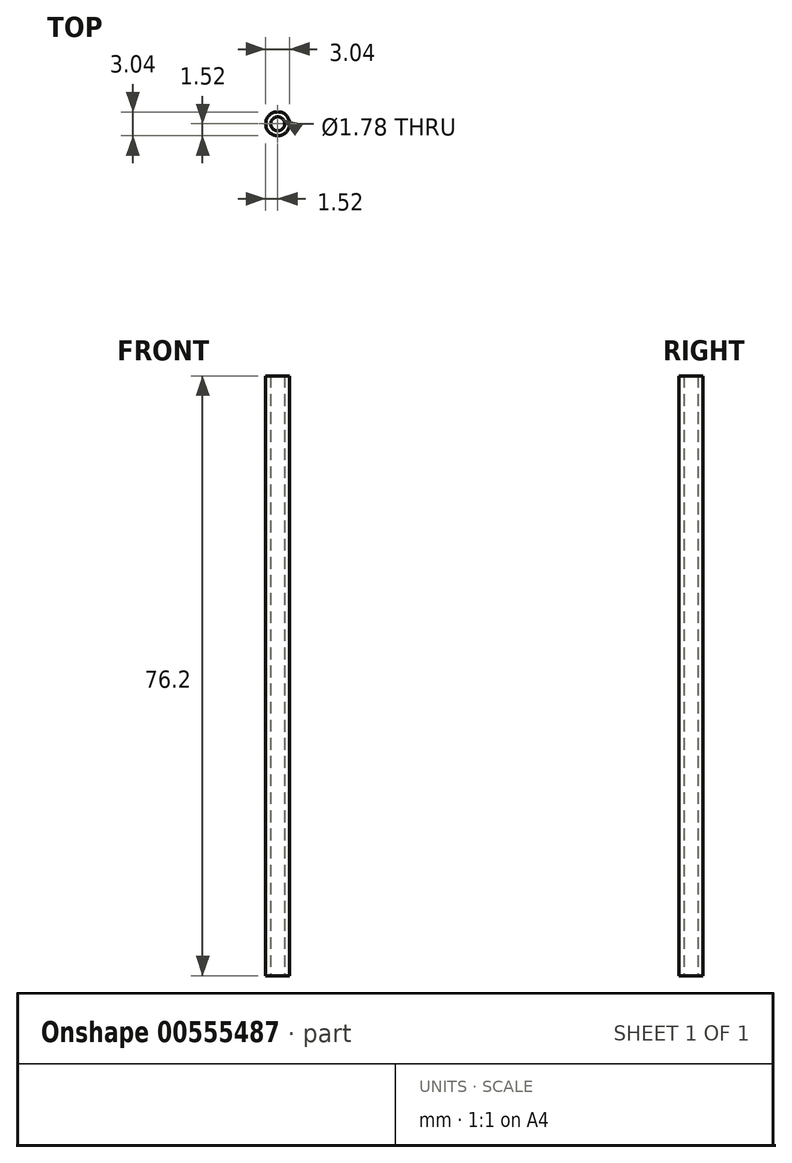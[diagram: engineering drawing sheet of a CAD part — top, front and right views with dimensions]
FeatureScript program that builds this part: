
annotation { "Feature Type Name" : "Feature", "Feature Type Description" : "" }
export const myFeature = defineFeature(function(context is Context, id is Id, definition is map)
    precondition{}
    {
        {
            var Q0;
            Q0=qCreatedBy(makeId("Top.planeOp"),FACE);
            var sketch = newSketch(context, id + "F0", { "sketchPlane" : qUnion([Q0])});
            skCircle(sketch, "E0", {"center": v(0, 0) * mm, "radius": 0.89 * mm});
            skCircle(sketch, "E1", {"center": v(0, 0) * mm, "radius": 1.52 * mm});
            skSolve(sketch);
        }
        {
            var Q0;
            Q0=makeQuery(id+"F0.imprint","IMPRINT",FACE,{"disambiguationData":[TD([[makeQuery(id+"F0.imprint","IMPRINT",EDGE,{"derivedFrom":sQuery(id+"F0.wireOp",EDGE,"E0")}),-1.0]])]});
            extrude(context, id + "F1", {"entities" : qUnion([Q0]), "endBound" : BoundingType.SYMMETRIC, "depth" : 76.2 * mm, "offsetDistance" : 25.4 * mm});
        }
    });
